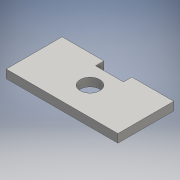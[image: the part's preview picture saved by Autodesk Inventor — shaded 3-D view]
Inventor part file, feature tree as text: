
AUTODESK INVENTOR PART (.ipt)
format: ipt  version: 2016 (Build 200138000, 138)  size: 107,520 bytes
history: native  units: mm
features: extrude x2, sketch x2, other x1
ambient origin geometry x8: Origin, YZ Plane, XZ Plane, XY Plane, X Axis, Y Axis, Z Axis, Center Point
bodies: Body1 (feature_tree)
feature tree (5):
  other  "Sólido1"
  extrude  "Extrusión1"  Depth=3.0mm
  extrude  "Extrusión2"  Depth=3.0mm TaperAngle=0.0deg
  sketch  "Boceto1"  dims[d0=3.0mm d1=0.0mm d3=5.0mm]
  sketch  "Boceto2"  dims[d4=5.0mm d5=3.0mm d6=0.0mm]
